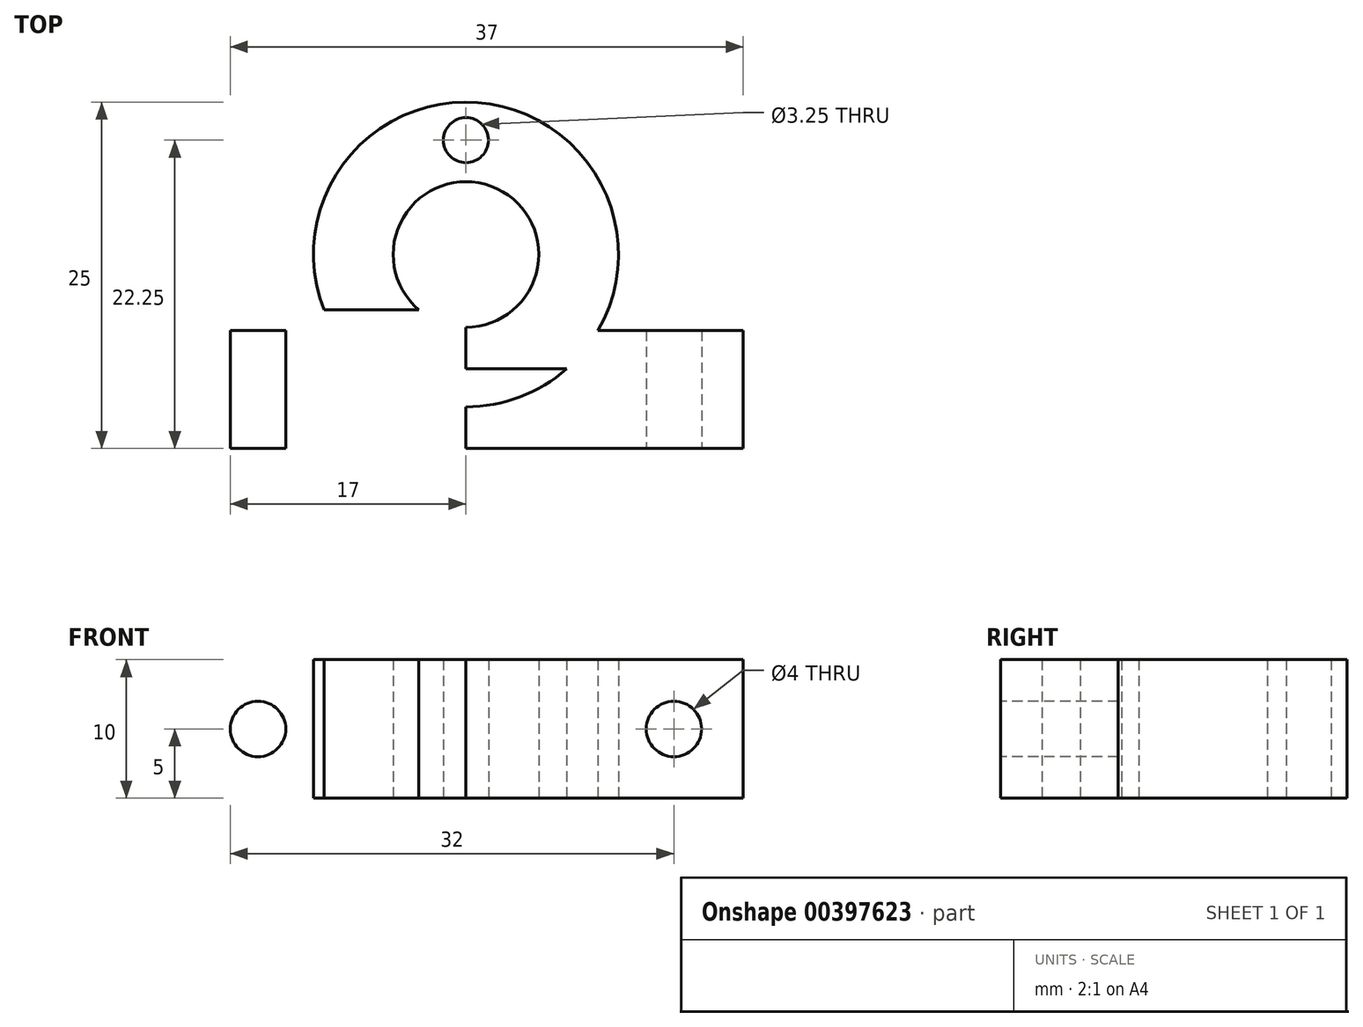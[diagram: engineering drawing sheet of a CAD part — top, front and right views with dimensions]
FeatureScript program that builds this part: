
annotation { "Feature Type Name" : "Feature", "Feature Type Description" : "" }
export const myFeature = defineFeature(function(context is Context, id is Id, definition is map)
    precondition{}
    {
        {
            var Q0;
            Q0=qCreatedBy(makeId("Top.planeOp"),FACE);
            var sketch = newSketch(context, id + "F0", { "sketchPlane" : qUnion([Q0])});
            skCircle(sketch, "E0", {"center": v(0, 0) * mm, "radius": 11 * mm});
            skCircle(sketch, "E1", {"center": v(0, 0) * mm, "radius": 5.25 * mm});
            skLineSegment(sketch, "E2", {"start": v(0, 0) * mm, "end": v(0, 11) * mm});
            skLineSegment(sketch, "E3", {"start": v(0, 0) * mm, "end": v(11, 0) * mm});
            skLineSegment(sketch, "E4", {"start": v(0, 11) * mm, "end": v(0, 5.5) * mm});
            skCircle(sketch, "E5", {"center": v(0, 8.25) * mm, "radius": 1.63 * mm});
            skCircle(sketch, "E6.MirrorC", {"center": v(0, -8.25) * mm, "radius": 1.63 * mm});
            skLineSegment(sketch, "E7.bottom", {"start": v(20, -11) * mm, "end": v(-20, -11) * mm});
            skLineSegment(sketch, "E7.top", {"start": v(20, -5.5) * mm, "end": v(-20, -5.5) * mm});
            skLineSegment(sketch, "E7.left", {"start": v(20, -11) * mm, "end": v(20, -5.5) * mm});
            skLineSegment(sketch, "E7.right", {"start": v(-20, -11) * mm, "end": v(-20, -5.5) * mm});
            skLineSegment(sketch, "E8", {"start": v(-20, -8.25) * mm, "end": v(20, -8.25) * mm});
            skLineSegment(sketch, "E9", {"start": v(0, -5.5) * mm, "end": v(0, -11) * mm});
            skLineSegment(sketch, "E10.bottom", {"start": v(-20, -11) * mm, "end": v(20, -11) * mm});
            skLineSegment(sketch, "E10.top", {"start": v(-20, -14) * mm, "end": v(20, -14) * mm});
            skLineSegment(sketch, "E10.left", {"start": v(-20, -11) * mm, "end": v(-20, -14) * mm});
            skLineSegment(sketch, "E10.right", {"start": v(20, -11) * mm, "end": v(20, -14) * mm});
            skSolve(sketch);
        }
        {
            var Q0;
            {var subQ0=sQuery(id+"F0.wireOp",EDGE,"E7.top");var subQ1=sQuery(id+"F0.wireOp",EDGE,"E0");var subQ2=makeQuery(id+"F0.imprint","INTERSECT",VERTEX,{"disambiguationData":[OD(0.0)],"derivedFrom":[subQ1,subQ0]});Q0=makeQuery(id+"F0.imprint","IMPRINT",FACE,{"disambiguationData":[TD([[makeQuery(id+"F0.imprint","IMPRINT",EDGE,{"disambiguationData":[TD([[subQ2,-1.0]])],"derivedFrom":subQ1}),-1.0]])]});}
            var Q1;
            {var subQ0=sQuery(id+"F0.wireOp",EDGE,"E7.bottom");var subQ5=sQuery(id+"F0.wireOp",EDGE,"E7.right");var subQ6=makeQuery(id+"F0.imprint","INTERSECT",VERTEX,{"derivedFrom":[subQ0,subQ5]});Q1=makeQuery(id+"F0.imprint","IMPRINT",FACE,{"disambiguationData":[TD([[makeQuery(id+"F0.imprint","IMPRINT",EDGE,{"disambiguationData":[TD([[subQ6,-1.0]])],"derivedFrom":subQ5}),-1.0]])]});}
            var Q2;
            {var subQ1=sQuery(id+"F0.wireOp",EDGE,"E0");var subQ6=sQuery(id+"F0.wireOp",EDGE,"E7.top");var subQ8=makeQuery(id+"F0.imprint","INTERSECT",VERTEX,{"disambiguationData":[OD(0.0)],"derivedFrom":[subQ1,subQ6]});Q2=makeQuery(id+"F0.imprint","IMPRINT",FACE,{"disambiguationData":[TD([[makeQuery(id+"F0.imprint","IMPRINT",EDGE,{"disambiguationData":[TD([[subQ8,-1.0]])],"derivedFrom":subQ1}),1.0]])]});}
            var Q3;
            {var subQ0=sQuery(id+"F0.wireOp",EDGE,"E9");var subQ5=sQuery(id+"F0.wireOp",EDGE,"E6.MirrorC");var subQ7=makeQuery(id+"F0.imprint","INTERSECT",VERTEX,{"disambiguationData":[OD(0.0)],"derivedFrom":[subQ5,subQ0]});Q3=makeQuery(id+"F0.imprint","IMPRINT",FACE,{"disambiguationData":[TD([[makeQuery(id+"F0.imprint","IMPRINT",EDGE,{"disambiguationData":[TD([[subQ7,-1.0]])],"derivedFrom":subQ5}),1.0]])]});}
            var Q4;
            {var subQ0=sQuery(id+"F0.wireOp",EDGE,"E9");var subQ5=sQuery(id+"F0.wireOp",EDGE,"E6.MirrorC");var subQ6=makeQuery(id+"F0.imprint","INTERSECT",VERTEX,{"disambiguationData":[OD(0.0)],"derivedFrom":[subQ5,subQ0]});Q4=makeQuery(id+"F0.imprint","IMPRINT",FACE,{"disambiguationData":[TD([[makeQuery(id+"F0.imprint","IMPRINT",EDGE,{"disambiguationData":[TD([[subQ6,1.0]])],"derivedFrom":subQ5}),1.0]])]});}
            var Q5;
            {var subQ1=sQuery(id+"F0.wireOp",EDGE,"E0");var subQ6=sQuery(id+"F0.wireOp",EDGE,"E7.top");var subQ8=makeQuery(id+"F0.imprint","INTERSECT",VERTEX,{"disambiguationData":[OD(1.0)],"derivedFrom":[subQ1,subQ6]});Q5=makeQuery(id+"F0.imprint","IMPRINT",FACE,{"disambiguationData":[TD([[makeQuery(id+"F0.imprint","IMPRINT",EDGE,{"disambiguationData":[TD([[subQ8,1.0]])],"derivedFrom":subQ1}),1.0]])]});}
            var Q6;
            {var subQ0=sQuery(id+"F0.wireOp",EDGE,"E7.top");var subQ1=sQuery(id+"F0.wireOp",EDGE,"E0");var subQ2=makeQuery(id+"F0.imprint","INTERSECT",VERTEX,{"disambiguationData":[OD(1.0)],"derivedFrom":[subQ1,subQ0]});Q6=makeQuery(id+"F0.imprint","IMPRINT",FACE,{"disambiguationData":[TD([[makeQuery(id+"F0.imprint","IMPRINT",EDGE,{"disambiguationData":[TD([[subQ2,1.0]])],"derivedFrom":subQ1}),-1.0]])]});}
            var Q7;
            {var subQ0=sQuery(id+"F0.wireOp",EDGE,"E7.bottom");var subQ5=sQuery(id+"F0.wireOp",EDGE,"E7.left");var subQ6=makeQuery(id+"F0.imprint","INTERSECT",VERTEX,{"derivedFrom":[subQ0,subQ5]});Q7=makeQuery(id+"F0.imprint","IMPRINT",FACE,{"disambiguationData":[TD([[makeQuery(id+"F0.imprint","IMPRINT",EDGE,{"disambiguationData":[TD([[subQ6,-1.0]])],"derivedFrom":subQ5}),1.0]])]});}
            var Q8;
            {var subQ0=sQuery(id+"F0.wireOp",EDGE,"E4");var subQ7=sQuery(id+"F0.wireOp",EDGE,"E0");var subQ11=makeQuery(id+"F0.imprint","INTERSECT",VERTEX,{"derivedFrom":[subQ7,subQ0]});Q8=makeQuery(id+"F0.imprint","IMPRINT",FACE,{"disambiguationData":[TD([[makeQuery(id+"F0.imprint","IMPRINT",EDGE,{"disambiguationData":[TD([[subQ11,-1.0]])],"derivedFrom":subQ7}),1.0]])]});}
            var Q9;
            {var subQ0=sQuery(id+"F0.wireOp",EDGE,"E3");var subQ1=sQuery(id+"F0.wireOp",EDGE,"E0");var subQ2=makeQuery(id+"F0.imprint","INTERSECT",VERTEX,{"derivedFrom":[subQ1,subQ0]});Q9=makeQuery(id+"F0.imprint","IMPRINT",FACE,{"disambiguationData":[TD([[makeQuery(id+"F0.imprint","IMPRINT",EDGE,{"disambiguationData":[TD([[subQ2,-1.0]])],"derivedFrom":subQ1}),1.0]])]});}
            var Q10;
            {var subQ3=sQuery(id+"F0.wireOp",EDGE,"E8");var subQ5=sQuery(id+"F0.wireOp",EDGE,"E7.right");var subQ7=makeQuery(id+"F0.imprint","INTERSECT",VERTEX,{"derivedFrom":[subQ5,subQ3]});Q10=makeQuery(id+"F0.imprint","IMPRINT",FACE,{"disambiguationData":[TD([[makeQuery(id+"F0.imprint","IMPRINT",EDGE,{"disambiguationData":[TD([[subQ7,-1.0]])],"derivedFrom":subQ3}),-1.0]])]});}
            var Q11;
            Q11=makeQuery(id+"F0.imprint","IMPRINT",FACE,{"disambiguationData":[TD([[makeQuery(id+"F0.imprint","IMPRINT",EDGE,{"derivedFrom":sQuery(id+"F0.wireOp",EDGE,"E10.top")}),1.0]])]});
            var Q12;
            {var subQ3=sQuery(id+"F0.wireOp",EDGE,"E8");var subQ5=sQuery(id+"F0.wireOp",EDGE,"E7.left");var subQ7=makeQuery(id+"F0.imprint","INTERSECT",VERTEX,{"derivedFrom":[subQ5,subQ3]});Q12=makeQuery(id+"F0.imprint","IMPRINT",FACE,{"disambiguationData":[TD([[makeQuery(id+"F0.imprint","IMPRINT",EDGE,{"disambiguationData":[TD([[subQ7,1.0]])],"derivedFrom":subQ3}),-1.0]])]});}
            extrude(context, id + "F1", {"entities" : qUnion([Q0, Q1, Q2, Q3, Q4, Q5, Q6, Q7, Q8, Q9, Q10, Q11, Q12]), "depth" : 10 * mm, "offsetDistance" : 25 * mm});
        }
        {
            var Q0;
            Q0=makeQuery(id+"F1.opExtrude","SWEPT_FACE",FACE,{"disambiguationData":[OSD([sQuery(id+"F0.wireOp",EDGE,"E10.top")])]});
            var sketch = newSketch(context, id + "F2", { "sketchPlane" : qUnion([Q0])});
            skLineSegment(sketch, "E11", {"start": v(-20, 5) * mm, "end": v(20, 5) * mm});
            skLineSegment(sketch, "E12", {"start": v(0, 10) * mm, "end": v(0, 0) * mm});
            skCircle(sketch, "E13", {"center": v(-15, 5) * mm, "radius": 2 * mm});
            skCircle(sketch, "E14.MirrorC", {"center": v(15, 5) * mm, "radius": 2 * mm});
            skSolve(sketch);
        }
        {
            var Q0;
            {var subQ0=sQuery(id+"F2.wireOp",EDGE,"E13");var subQ1=sQuery(id+"F2.wireOp",EDGE,"E11");var subQ2=makeQuery(id+"F2.imprint","INTERSECT",VERTEX,{"disambiguationData":[OD(0.0)],"derivedFrom":[subQ1,subQ0]});Q0=makeQuery(id+"F2.imprint","IMPRINT",FACE,{"disambiguationData":[TD([[makeQuery(id+"F2.imprint","IMPRINT",EDGE,{"disambiguationData":[TD([[subQ2,-1.0]])],"derivedFrom":subQ1}),1.0]])]});}
            var Q1;
            {var subQ0=sQuery(id+"F2.wireOp",EDGE,"E13");var subQ1=sQuery(id+"F2.wireOp",EDGE,"E11");var subQ2=makeQuery(id+"F2.imprint","INTERSECT",VERTEX,{"disambiguationData":[OD(0.0)],"derivedFrom":[subQ1,subQ0]});Q1=makeQuery(id+"F2.imprint","IMPRINT",FACE,{"disambiguationData":[TD([[makeQuery(id+"F2.imprint","IMPRINT",EDGE,{"disambiguationData":[TD([[subQ2,-1.0]])],"derivedFrom":subQ1}),-1.0]])]});}
            var Q2;
            {var subQ0=sQuery(id+"F2.wireOp",EDGE,"E14.MirrorC");var subQ1=sQuery(id+"F2.wireOp",EDGE,"E11");var subQ2=makeQuery(id+"F2.imprint","INTERSECT",VERTEX,{"disambiguationData":[OD(0.0)],"derivedFrom":[subQ1,subQ0]});Q2=makeQuery(id+"F2.imprint","IMPRINT",FACE,{"disambiguationData":[TD([[makeQuery(id+"F2.imprint","IMPRINT",EDGE,{"disambiguationData":[TD([[subQ2,-1.0]])],"derivedFrom":subQ1}),1.0]])]});}
            var Q3;
            {var subQ0=sQuery(id+"F2.wireOp",EDGE,"E14.MirrorC");var subQ1=sQuery(id+"F2.wireOp",EDGE,"E11");var subQ2=makeQuery(id+"F2.imprint","INTERSECT",VERTEX,{"disambiguationData":[OD(0.0)],"derivedFrom":[subQ1,subQ0]});Q3=makeQuery(id+"F2.imprint","IMPRINT",FACE,{"disambiguationData":[TD([[makeQuery(id+"F2.imprint","IMPRINT",EDGE,{"disambiguationData":[TD([[subQ2,-1.0]])],"derivedFrom":subQ1}),-1.0]])]});}
            extrude(context, id + "F3", {"entities" : qUnion([Q0, Q1, Q2, Q3]), "operationType" : NewBodyOperationType.REMOVE, "oppositeDirection" : true, "depth" : 10 * mm, "offsetDistance" : 25 * mm});
        }
    });
